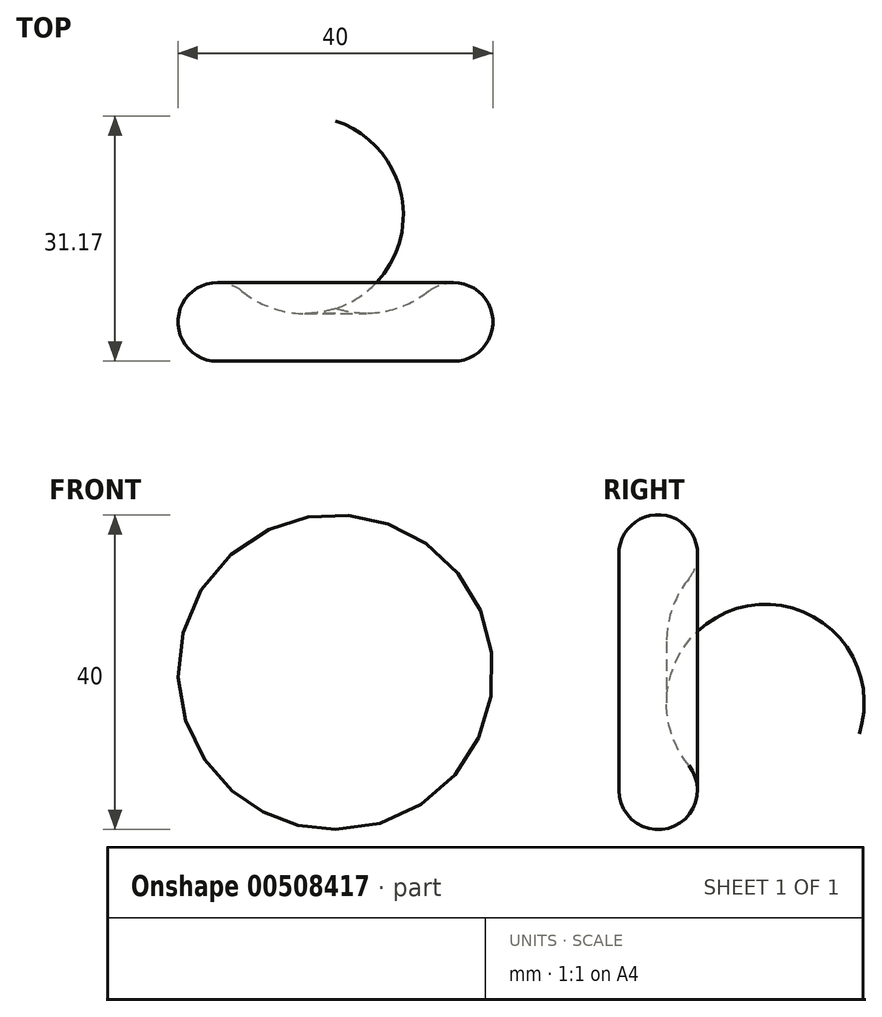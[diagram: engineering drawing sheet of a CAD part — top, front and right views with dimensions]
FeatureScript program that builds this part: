
annotation { "Feature Type Name" : "Feature", "Feature Type Description" : "" }
export const myFeature = defineFeature(function(context is Context, id is Id, definition is map)
    precondition{}
    {
        {
            var Q0;
            Q0=qCreatedBy(makeId("Top.planeOp"),FACE);
            var sketch = newSketch(context, id + "F0", { "sketchPlane" : qUnion([Q0])});
            skArc(sketch, "E0", {"start": v(-11.85, 8.88) * mm, "mid": v(-19.71, 6.67) * mm, "end": v(-15, 0) * mm});
            skArc(sketch, "E1", {"start": v(-11.85, 8.88) * mm, "mid": v(-6.2, 6.27) * mm, "end": v(0, 6.7) * mm});
            skLineSegment(sketch, "E2", {"start": v(-15, 0) * mm, "end": v(0, 0) * mm});
            skLineSegment(sketch, "E3", {"start": v(0, 0) * mm, "end": v(0, 6.7) * mm});
            skSolve(sketch);
        }
        {
            var Q0;
            Q0=makeQuery(id+"F0.imprint","IMPRINT",FACE,{"disambiguationData":[TD([[makeQuery(id+"F0.imprint","IMPRINT",EDGE,{"derivedFrom":sQuery(id+"F0.wireOp",EDGE,"E0")}),1.0]])]});
            var Q1;
            Q1=sQuery(id+"F0.wireOp",EDGE,"E3");
            revolve(context, id + "F1", {"entities" : qUnion([Q0]), "axis" : qUnion([Q1]), "revolveType" : RevolveType.FULL});
        }
    });
